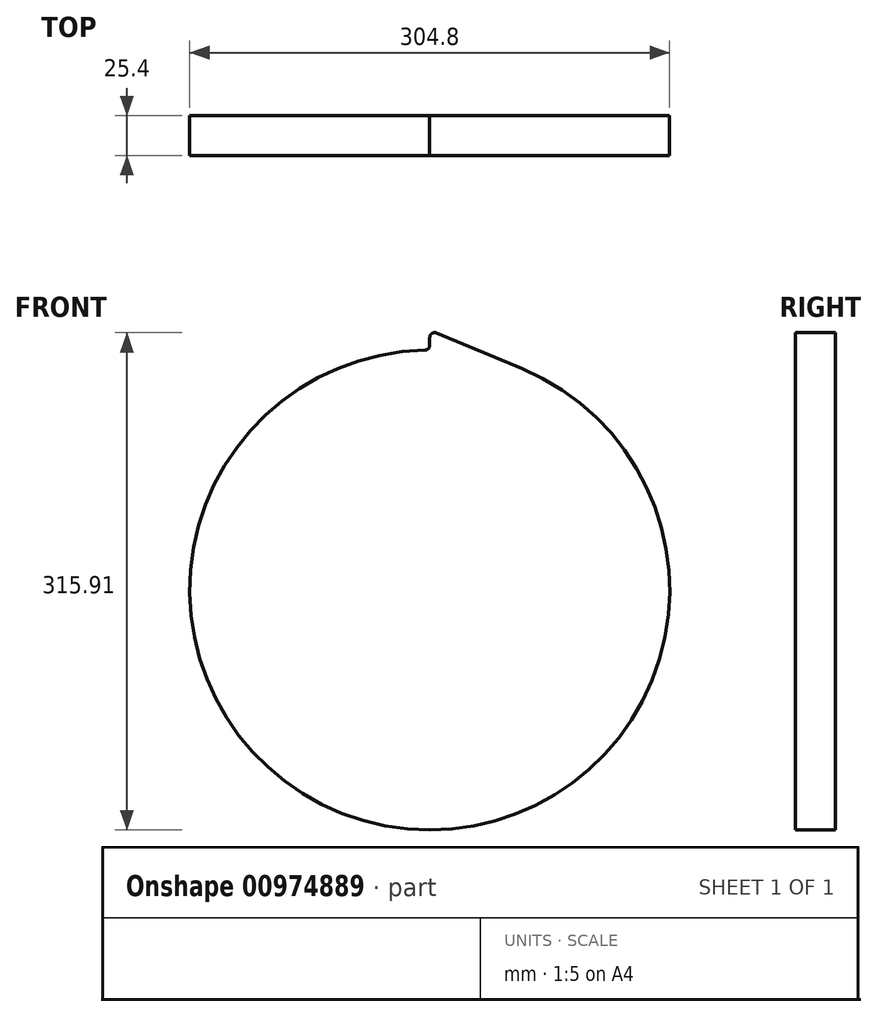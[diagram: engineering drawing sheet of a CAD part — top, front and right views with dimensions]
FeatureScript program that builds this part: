
annotation { "Feature Type Name" : "Feature", "Feature Type Description" : "" }
export const myFeature = defineFeature(function(context is Context, id is Id, definition is map)
    precondition{}
    {
        {
            var Q0;
            Q0=qCreatedBy(makeId("Front.planeOp"),FACE);
            var sketch = newSketch(context, id + "F0", { "sketchPlane" : qUnion([Q0])});
            skCircle(sketch, "E0", {"center": v(0, 0) * mm, "radius": 152.4 * mm});
            skLineSegment(sketch, "E1", {"start": v(0, 165.1) * mm, "end": v(0, 152.4) * mm});
            skLineSegment(sketch, "E2", {"start": v(0, 152.4) * mm, "end": v(-25.4, 152.4) * mm, "construction": true});
            skLineSegment(sketch, "E3", {"start": v(0, 165.1) * mm, "end": v(58.62, 140.68) * mm});
            skSolve(sketch);
        }
        {
            var Q0;
            {var subQ0=sQuery(id+"F0.wireOp",EDGE,"E0");var subQ1=makeQuery(id+"F0.imprint","INTERSECT",VERTEX,{"derivedFrom":[subQ0,sQuery(id+"F0.wireOp",EDGE,"E1")]});Q0=makeQuery(id+"F0.imprint","IMPRINT",FACE,{"disambiguationData":[TD([[makeQuery(id+"F0.imprint","IMPRINT",EDGE,{"disambiguationData":[TD([[subQ1,1.0]])],"derivedFrom":subQ0}),1.0]])]});}
            var Q1;
            {var subQ0=sQuery(id+"F0.wireOp",EDGE,"E1");Q1=makeQuery(id+"F0.imprint","IMPRINT",FACE,{"disambiguationData":[TD([[makeQuery(id+"F0.imprint","IMPRINT",EDGE,{"derivedFrom":subQ0}),1.0]])]});}
            extrude(context, id + "F1", {"entities" : qUnion([Q0, Q1]), "depth" : 25.4 * mm, "offsetDistance" : 25.4 * mm});
        }
        {
            var Q0;
            Q0=makeQuery(id+"F1.opExtrude","SWEPT_EDGE",EDGE,{"disambiguationData":[OSD([sQuery(id+"F0.wireOp",EDGE,"E0"),sQuery(id+"F0.wireOp",EDGE,"E1")])]});
            fillet(context, id + "F2", {"entities" : qUnion([Q0]), "radius" : 3.17 * mm, "tangentPropagation" : true, "allowEdgeOverflow" : false});
        }
        {
            var Q0;
            Q0=makeQuery(id+"F1.opExtrude","SWEPT_EDGE",EDGE,{"disambiguationData":[OSD([sQuery(id+"F0.wireOp",EDGE,"E1"),sQuery(id+"F0.wireOp",EDGE,"E3")])]});
            fillet(context, id + "F3", {"entities" : qUnion([Q0]), "radius" : 3.17 * mm, "tangentPropagation" : true, "allowEdgeOverflow" : false});
        }
    });
